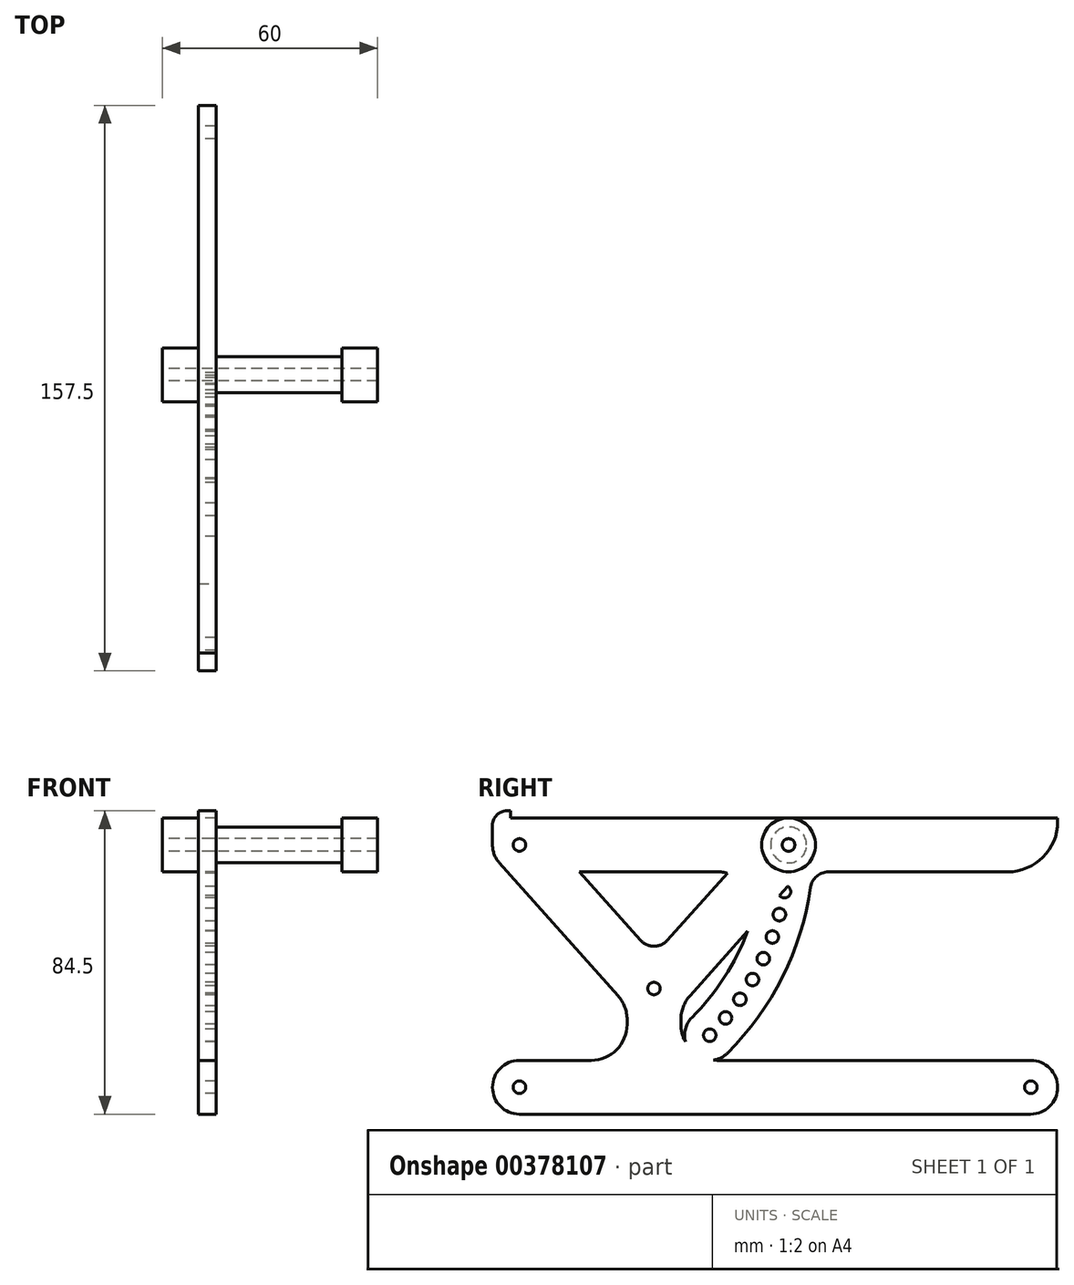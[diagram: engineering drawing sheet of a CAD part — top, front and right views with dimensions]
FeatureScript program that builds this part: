
annotation { "Feature Type Name" : "Feature", "Feature Type Description" : "" }
export const myFeature = defineFeature(function(context is Context, id is Id, definition is map)
    precondition{}
    {
        {
            var Q0;
            Q0=qCreatedBy(makeId("Right.planeOp"),FACE);
            var sketch = newSketch(context, id + "F0", { "sketchPlane" : qUnion([Q0])});
            skLineSegment(sketch, "E0", {"start": v(-75, 7.5) * mm, "end": v(75, 7.5) * mm});
            skLineSegment(sketch, "E1", {"start": v(75, 7.5) * mm, "end": v(75, 6.5) * mm});
            skLineSegment(sketch, "E2", {"start": v(61, -7.5) * mm, "end": v(11.1, -7.5) * mm});
            skLineSegment(sketch, "E3.trimOffspring", {"start": v(-19.7, -7.5) * mm, "end": v(-75, -7.5) * mm});
            skArc(sketch, "E4", {"start": v(-82.5, 0) * mm, "mid": v(-80.3, -5.3) * mm, "end": v(-75, -7.5) * mm});
            skArc(sketch, "E5", {"start": v(-17.02, -57.98) * mm, "mid": v(-1.7, -36.76) * mm, "end": v(6.15, -11.78) * mm});
            skArc(sketch, "E6", {"start": v(-26.92, -48.08) * mm, "mid": v(-16.88, -35.3) * mm, "end": v(-10.17, -20.52) * mm});
            skArc(sketch, "E7", {"start": v(-26.92, -48.08) * mm, "mid": v(-26.92, -57.98) * mm, "end": v(-17.02, -57.98) * mm});
            skPoint(sketch, "E8.visualSharp", {"position": v(-7.41, -7.5) * mm});
            skArc(sketch, "E8.filletArc", {"start": v(-10.17, -20.52) * mm, "mid": v(-11.64, -11.6) * mm, "end": v(-19.7, -7.5) * mm});
            skPoint(sketch, "E9.visualSharp", {"position": v(6.66, -7.5) * mm});
            skArc(sketch, "E9.filletArc", {"start": v(11.1, -7.5) * mm, "mid": v(7.83, -8.72) * mm, "end": v(6.15, -11.78) * mm});
            skCircle(sketch, "E10", {"center": v(-75, 0) * mm, "radius": 1.75 * mm});
            skLineSegment(sketch, "E11", {"start": v(-75, 0) * mm, "end": v(-17.02, -57.98) * mm, "construction": true});
            skLineSegment(sketch, "E12", {"start": v(-75, 0) * mm, "end": v(-3.99, -41) * mm, "construction": true});
            skLineSegment(sketch, "E13", {"start": v(-75, 0) * mm, "end": v(-7.83, -47.03) * mm, "construction": true});
            skLineSegment(sketch, "E14", {"start": v(-75, 0) * mm, "end": v(2.05, -28.05) * mm, "construction": true});
            skLineSegment(sketch, "E15", {"start": v(-75, 0) * mm, "end": v(-0.68, -34.65) * mm, "construction": true});
            skLineSegment(sketch, "E16", {"start": v(-75, 0) * mm, "end": v(-12.18, -52.7) * mm, "construction": true});
            skArc(sketch, "E17", {"start": v(-27.14, -57.75) * mm, "mid": v(-5.61, -28.47) * mm, "end": v(-0.38, 7.5) * mm, "construction": true});
            skCircle(sketch, "E18", {"center": v(-21.97, -53.03) * mm, "radius": 1.75 * mm});
            skCircle(sketch, "E19", {"center": v(-17.55, -48.2) * mm, "radius": 1.75 * mm});
            skCircle(sketch, "E20", {"center": v(-13.56, -43.02) * mm, "radius": 1.75 * mm});
            skCircle(sketch, "E21", {"center": v(-10.05, -37.5) * mm, "radius": 1.75 * mm});
            skCircle(sketch, "E22", {"center": v(-7.03, -31.7) * mm, "radius": 1.75 * mm});
            skCircle(sketch, "E23", {"center": v(-4.52, -25.65) * mm, "radius": 1.75 * mm});
            skCircle(sketch, "E24", {"center": v(0, 0) * mm, "radius": 1.75 * mm});
            skLineSegment(sketch, "E25", {"start": v(-75, 0) * mm, "end": v(4.2, -21.22) * mm, "construction": true});
            skLineSegment(sketch, "E26", {"start": v(-75, 0) * mm, "end": v(5.75, -14.24) * mm, "construction": true});
            skCircle(sketch, "E27", {"center": v(-2.56, -19.41) * mm, "radius": 1.75 * mm});
            skCircle(sketch, "E28", {"center": v(-1.14, -13.02) * mm, "radius": 1.75 * mm});
            skPoint(sketch, "E29.visualSharp", {"position": v(75, -7.5) * mm});
            skArc(sketch, "E29.filletArc", {"start": v(61, -7.5) * mm, "mid": v(70.9, -3.4) * mm, "end": v(75, 6.5) * mm});
            skLineSegment(sketch, "E30", {"start": v(-82.5, 0) * mm, "end": v(-82.5, 5.5) * mm});
            skLineSegment(sketch, "E31", {"start": v(-78.5, 9.5) * mm, "end": v(-77.5, 9.5) * mm});
            skLineSegment(sketch, "E32", {"start": v(-75, 7.5) * mm, "end": v(-77.5, 7.5) * mm});
            skLineSegment(sketch, "E33", {"start": v(-77.5, 7.5) * mm, "end": v(-77.5, 9.5) * mm});
            skPoint(sketch, "E34.visualSharp", {"position": v(-82.5, 9.5) * mm});
            skArc(sketch, "E34.filletArc", {"start": v(-78.5, 9.5) * mm, "mid": v(-81.33, 8.33) * mm, "end": v(-82.5, 5.5) * mm});
            skSolve(sketch);
        }
        {
            var Q0;
            Q0 = qSketchRegion(id + "F0", true);
            extrude(context, id + "F1", {"entities" : qUnion([Q0]), "depth" : 5 * mm});
        }
        {
            var Q0;
            Q0=qCreatedBy(makeId("Right.planeOp"),FACE);
            var sketch = newSketch(context, id + "F2", { "sketchPlane" : qUnion([Q0])});
            skArc(sketch, "E35", {"start": v(-69.4, 5) * mm, "mid": v(-80, 5.6) * mm, "end": v(-80.6, -5) * mm});
            skArc(sketch, "E36", {"start": v(5.6, -5) * mm, "mid": v(5, 5.6) * mm, "end": v(-5.6, 5) * mm});
            skLineSegment(sketch, "E37", {"start": v(-75, 0) * mm, "end": v(-37.5, -42) * mm, "construction": true});
            skLineSegment(sketch, "E38", {"start": v(-37.5, -42) * mm, "end": v(0, 0) * mm, "construction": true});
            skLineSegment(sketch, "E39", {"start": v(-37.5, -40) * mm, "end": v(-37.5, -75) * mm, "construction": true});
            skLineSegment(sketch, "E40.left", {"start": v(-30, -50) * mm, "end": v(-30, -48.68) * mm});
            skLineSegment(sketch, "E40.right", {"start": v(-45, -50) * mm, "end": v(-45, -48.68) * mm});
            skLineSegment(sketch, "E41", {"start": v(-80.6, -5) * mm, "end": v(-47.54, -42.02) * mm});
            skLineSegment(sketch, "E42", {"start": v(-69.4, 5) * mm, "end": v(-41.23, -26.56) * mm});
            skLineSegment(sketch, "E43", {"start": v(-5.6, 5) * mm, "end": v(-33.77, -26.56) * mm});
            skLineSegment(sketch, "E44", {"start": v(5.6, -5) * mm, "end": v(-27.46, -42.02) * mm});
            skArc(sketch, "E45.filletArc", {"start": v(-41.23, -26.56) * mm, "mid": v(-37.5, -28.23) * mm, "end": v(-33.77, -26.56) * mm});
            skPoint(sketch, "E46.visualSharp", {"position": v(-45, -44.86) * mm});
            skArc(sketch, "E46.filletArc", {"start": v(-45, -48.68) * mm, "mid": v(-45.66, -45.11) * mm, "end": v(-47.54, -42.02) * mm});
            skPoint(sketch, "E47.visualSharp", {"position": v(-30, -44.86) * mm});
            skArc(sketch, "E47.filletArc", {"start": v(-27.46, -42.02) * mm, "mid": v(-29.34, -45.11) * mm, "end": v(-30, -48.68) * mm});
            skCircle(sketch, "E48", {"center": v(-75, 0) * mm, "radius": 1.75 * mm});
            skCircle(sketch, "E49", {"center": v(0, 0) * mm, "radius": 1.75 * mm});
            skLineSegment(sketch, "E50.bottom", {"start": v(-75, -60) * mm, "end": v(-55, -60) * mm});
            skLineSegment(sketch, "E50.top", {"start": v(-75, -75) * mm, "end": v(67.5, -75) * mm});
            skLineSegment(sketch, "E50.right", {"start": v(75, -67.5) * mm, "end": v(75, -67.5) * mm});
            skLineSegment(sketch, "E51.trimOffspring", {"start": v(-20, -60) * mm, "end": v(67.5, -60) * mm});
            skPoint(sketch, "E52.visualSharp", {"position": v(-45, -60) * mm});
            skArc(sketch, "E52.filletArc", {"start": v(-55, -60) * mm, "mid": v(-47.93, -57.07) * mm, "end": v(-45, -50) * mm});
            skPoint(sketch, "E53.visualSharp", {"position": v(-30, -60) * mm});
            skArc(sketch, "E53.filletArc", {"start": v(-30, -50) * mm, "mid": v(-27.07, -57.07) * mm, "end": v(-20, -60) * mm});
            skArc(sketch, "E54", {"start": v(-75, -60) * mm, "mid": v(-82.5, -67.5) * mm, "end": v(-75, -75) * mm});
            skPoint(sketch, "E55.visualSharp", {"position": v(75, -60) * mm});
            skArc(sketch, "E55.filletArc", {"start": v(75, -67.5) * mm, "mid": v(72.8, -62.2) * mm, "end": v(67.5, -60) * mm});
            skLineSegment(sketch, "E56", {"start": v(-75, -60) * mm, "end": v(-75, -75) * mm, "construction": true});
            skCircle(sketch, "E57", {"center": v(-75, -67.5) * mm, "radius": 1.75 * mm});
            skCircle(sketch, "E58", {"center": v(-37.5, -40) * mm, "radius": 1.75 * mm});
            skCircle(sketch, "E59", {"center": v(67.5, -67.5) * mm, "radius": 1.75 * mm});
            skPoint(sketch, "E60.visualSharp", {"position": v(75, -75) * mm});
            skArc(sketch, "E60.filletArc", {"start": v(67.5, -75) * mm, "mid": v(72.8, -72.8) * mm, "end": v(75, -67.5) * mm});
            skSolve(sketch);
        }
        {
            var Q0;
            Q0 = qSketchRegion(id + "F2", true);
            extrude(context, id + "F3", {"entities" : qUnion([Q0]), "depth" : 5 * mm});
        }
        {
            var Q0;
            Q0=qCreatedBy(makeId("Right.planeOp"),FACE);
            var sketch = newSketch(context, id + "F4", { "sketchPlane" : qUnion([Q0])});
            skCircle(sketch, "E61", {"center": v(0, 0) * mm, "radius": 5 * mm});
            skSolve(sketch);
        }
        {
            var Q0;
            Q0 = qSketchRegion(id + "F4", true);
            extrude(context, id + "F5", {"entities" : qUnion([Q0]), "depth" : 40 * mm});
        }
        {
            var Q0;
            Q0=makeQuery(id+"F5.opExtrude","CAP_FACE",FACE,{"disambiguationData":[OSD([sQuery(id+"F4.wireOp",EDGE,"E61")])],"isStart":false});
            var sketch = newSketch(context, id + "F6", { "sketchPlane" : qUnion([Q0])});
            skCircle(sketch, "E62", {"center": v(0, 0) * mm, "radius": 7.5 * mm});
            skSolve(sketch);
        }
        {
            var Q0;
            Q0 = qSketchRegion(id + "F6", true);
            extrude(context, id + "F7", {"entities" : qUnion([Q0]), "operationType" : NewBodyOperationType.ADD, "depth" : 10 * mm});
        }
        {
            var Q0;
            Q0=makeQuery(id+"F5.opExtrude","CAP_FACE",FACE,{"disambiguationData":[OSD([sQuery(id+"F4.wireOp",EDGE,"E61")])],"isStart":true});
            var sketch = newSketch(context, id + "F8", { "sketchPlane" : qUnion([Q0])});
            skCircle(sketch, "E63", {"center": v(0, 0) * mm, "radius": 7.5 * mm});
            skSolve(sketch);
        }
        {
            var Q0;
            Q0 = qSketchRegion(id + "F8", true);
            extrude(context, id + "F9", {"entities" : qUnion([Q0]), "operationType" : NewBodyOperationType.ADD, "depth" : 10 * mm});
        }
        {
            var Q0;
            Q0=makeQuery(id+"F9.opExtrude","CAP_FACE",FACE,{"disambiguationData":[OSD([sQuery(id+"F8.wireOp",EDGE,"E63")])],"isStart":false});
            var sketch = newSketch(context, id + "F10", { "sketchPlane" : qUnion([Q0])});
            skCircle(sketch, "E64", {"center": v(0, 0) * mm, "radius": 1.75 * mm});
            skSolve(sketch);
        }
        {
            var Q0;
            Q0 = qSketchRegion(id + "F10", true);
            extrude(context, id + "F11", {"entities" : qUnion([Q0]), "operationType" : NewBodyOperationType.REMOVE, "endBound" : BoundingType.THROUGH_ALL, "oppositeDirection" : true, "depth" : 25 * mm});
        }
    });
